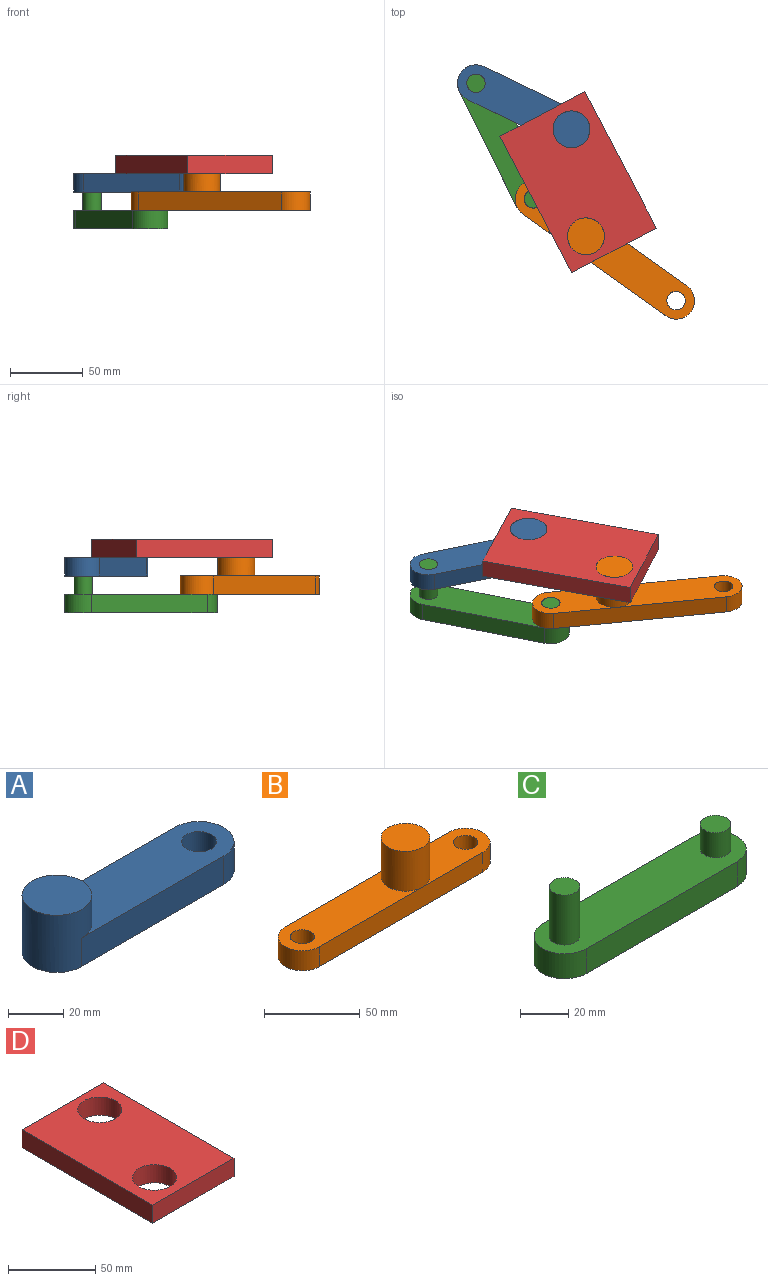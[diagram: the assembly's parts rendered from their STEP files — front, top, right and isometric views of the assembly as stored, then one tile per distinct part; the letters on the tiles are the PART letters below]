
ASSEMBLY  parts=4 mates=4
PART A: 8 faces, bbox 98.4x25.4x25.4 mm
  f0: plane 73.03x12.7mm, normal (0,-1,0), area 927.4mm2, adj f1,f4,f5,f6
  f1: cylinder r=12.7mm len=25.4mm, axis (0,0,-1), area 506.7mm2, adj f0,f2,f4,f5
  f2: plane 73.03x12.7mm, normal (0,1,0), area 927.4mm2, adj f1,f4,f5,f6
  f3: cylinder r=6.35mm len=12.7mm, axis (0,0,-1), area 506.7mm2, adj f4,f5
  f4: plane 85.73x25.4mm, normal (0,0,1), area 1728.2mm2, adj f0,f1,f2,f3,f6
  f5: plane 98.43x25.4mm, normal (0,0,-1), area 2234.9mm2, adj f0,f1,f2,f3,f6
  f6: cylinder r=12.7mm len=25.4mm, axis (0,0,-1), area 1520.1mm2, adj f0,f2,f4,f5,f7
  f7: plane 25.4x25.4mm, normal (0,0,1), area 506.7mm2, adj f6
PART B: 11 faces, bbox 146.1x25.4x38.1 mm
  f0: cylinder r=12.7mm len=25.4mm, axis (0,0,-1), area 2026.8mm2, adj f1,f7,f10
  f1: plane 25.4x25.4mm, normal (0,0,1), area 506.7mm2, adj f0
  f2: plane 146.05x25.4mm, normal (0,0,-1), area 3317.9mm2, adj f3,f4,f5,f6,f8,f9
  f3: cylinder r=12.7mm len=25.4mm, axis (0,0,-1), area 506.7mm2, adj f2,f4,f6,f7
  f4: plane 120.65x12.7mm, normal (0,-1,0), area 1532.3mm2, adj f2,f3,f7,f8,f10
  f5: cylinder r=6.35mm len=12.7mm, axis (0,0,-1), area 506.7mm2, adj f2,f7
  f6: plane 120.65x12.7mm, normal (0,1,0), area 1532.3mm2, adj f2,f3,f7,f8,f10
  f7: plane 88.9x25.4mm, normal (0,0,1), area 1808.8mm2, adj f0,f3,f4,f5,f6
  f8: cylinder r=12.7mm len=25.4mm, axis (0,0,-1), area 506.7mm2, adj f2,f4,f6,f10
  f9: cylinder r=6.35mm len=12.7mm, axis (0,0,-1), area 506.7mm2, adj f2,f10
  f10: plane 57.15x25.4mm, normal (0,0,1), area 1002.4mm2, adj f0,f4,f6,f8,f9
PART C: 10 faces, bbox 114.3x25.4x38.1 mm
  f0: cylinder r=12.7mm len=25.4mm, axis (0,0,-1), area 506.7mm2, adj f1,f3,f4,f5
  f1: plane 88.9x12.7mm, normal (0,-1,0), area 1129mm2, adj f0,f2,f4,f5
  f2: cylinder r=12.7mm len=25.4mm, axis (0,0,-1), area 506.7mm2, adj f1,f3,f4,f5
  f3: plane 88.9x12.7mm, normal (0,1,0), area 1129mm2, adj f0,f2,f4,f5
  f4: plane 114.3x25.4mm, normal (0,0,1), area 2511.4mm2, adj f0,f1,f2,f3,f6,f8
  f5: plane 114.3x25.4mm, normal (0,0,-1), area 2764.8mm2, adj f0,f1,f2,f3
  f6: cylinder r=6.35mm len=25.4mm, axis (0,0,-1), area 1013.4mm2, adj f4,f7
  f7: plane 12.7x12.7mm, normal (0,0,1), area 126.7mm2, adj f6
  f8: cylinder r=6.35mm len=12.7mm, axis (0,0,-1), area 506.7mm2, adj f4,f9
  f9: plane 12.7x12.7mm, normal (0,0,1), area 126.7mm2, adj f8
PART D: 8 faces, bbox 66x106.2x12.7 mm
  f0: plane 106.15x12.7mm, normal (-1,0,0), area 1348.1mm2, adj f1,f4,f6,f7
  f1: plane 66.04x12.7mm, normal (0,-1,0), area 838.7mm2, adj f0,f2,f6,f7
  f2: plane 106.15x12.7mm, normal (1,0,0), area 1348.1mm2, adj f1,f4,f6,f7
  f3: cylinder r=12.7mm len=25.4mm, axis (0,0,-1), area 1013.4mm2, adj f6,f7
  f4: plane 66.04x12.7mm, normal (0,1,0), area 838.7mm2, adj f0,f2,f6,f7
  f5: cylinder r=12.7mm len=25.4mm, axis (0,0,-1), area 1013.4mm2, adj f6,f7
  f6: plane 106.15x66.04mm, normal (0,0,1), area 5996.9mm2, adj f0,f1,f2,f3,f4,f5
  f7: plane 106.15x66.04mm, normal (0,0,-1), area 5996.9mm2, adj f0,f1,f2,f3,f4,f5
PLACE A rot(axis=(0,0,1),154.2deg) t=(45.72,-99.58,-150.02)mm
PLACE B rot(axis=(0,0,1),144.5deg) t=(111.21,-136.78,-162.67)mm
PLACE C rot(axis=(0,0,-1),63.5deg) t=(11.26,-34.48,-175.42)mm
PLACE D rot(axis=(0,0,-1),152.3deg) t=(105.93,-265.8,-137.32)mm
MATE cylindrical D.f3 <-> A.f6  axis (0,0,1) through (45.72,-99.58,-124.62)mm
MATE cylindrical B.f0 <-> D.f5  axis (0,0,1) through (55.75,-173.22,-124.57)mm
MATE cylindrical C.f0 <-> A.f3  axis (0,0,1) through (-20.02,-67.79,-137.32)mm
MATE cylindrical B.f8 <-> C.f2  axis (0,0,1) through (19.58,-147.38,-149.97)mm
